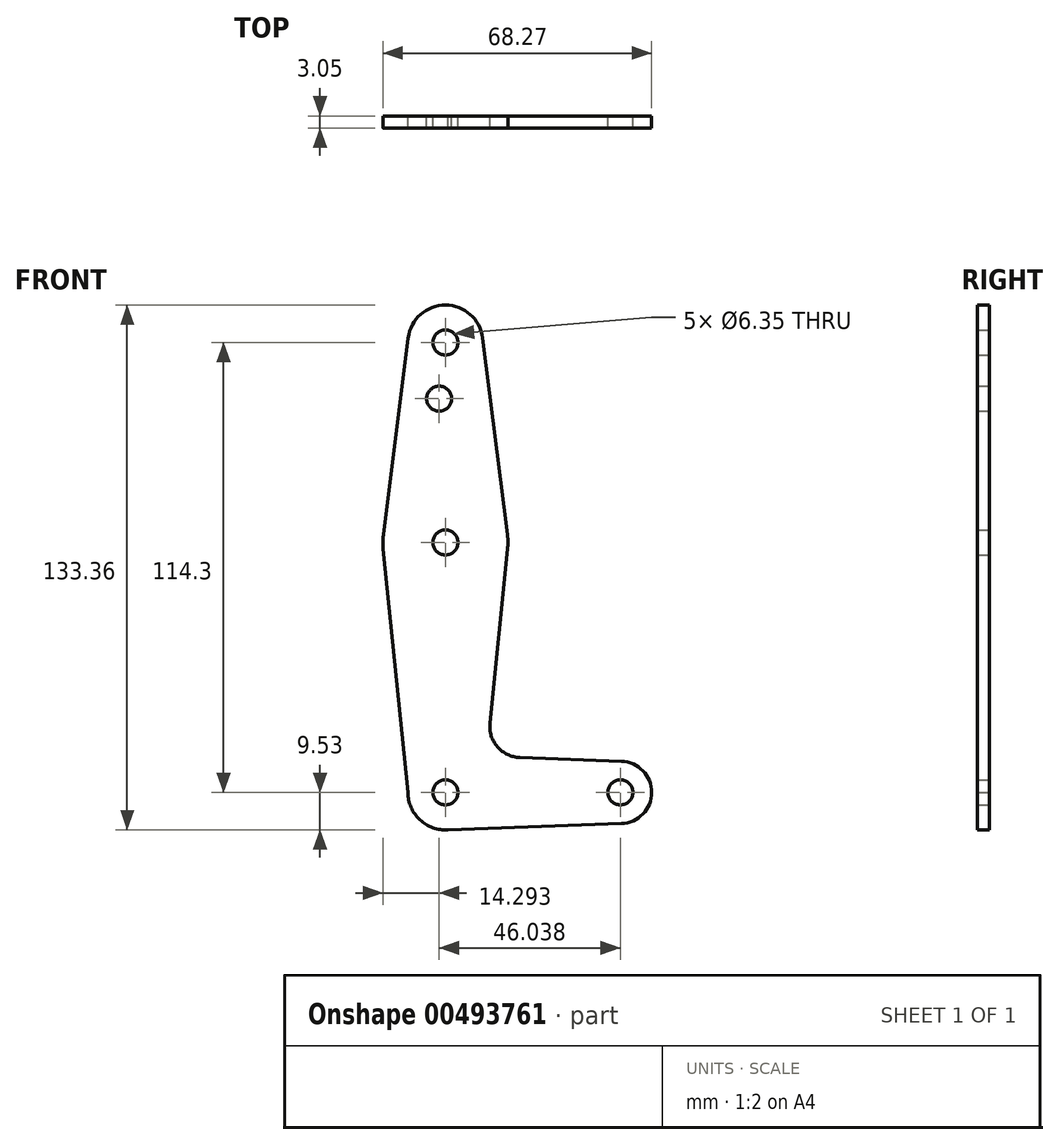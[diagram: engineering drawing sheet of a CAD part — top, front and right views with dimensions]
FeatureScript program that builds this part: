
annotation { "Feature Type Name" : "Feature", "Feature Type Description" : "" }
export const myFeature = defineFeature(function(context is Context, id is Id, definition is map)
    precondition{}
    {
        {
            var Q0;
            Q0=qCreatedBy(makeId("Front.planeOp"),FACE);
            var sketch = newSketch(context, id + "F0", { "sketchPlane" : qUnion([Q0])});
            skLineSegment(sketch, "E0", {"start": v(0, 0) * mm, "end": v(0, 114.3) * mm, "construction": true});
            skCircle(sketch, "E1", {"center": v(0, 114.3) * mm, "radius": 9.53 * mm});
            skCircle(sketch, "E2", {"center": v(0, 63.5) * mm, "radius": 15.88 * mm});
            skCircle(sketch, "E3", {"center": v(0, 0) * mm, "radius": 9.53 * mm});
            skLineSegment(sketch, "E4", {"start": v(0, 0) * mm, "end": v(44.45, 0) * mm, "construction": true});
            skCircle(sketch, "E5", {"center": v(44.45, 0) * mm, "radius": 7.94 * mm});
            skLineSegment(sketch, "E6", {"start": v(-15.75, 65.48) * mm, "end": v(-9.45, 115.5) * mm});
            skLineSegment(sketch, "E7", {"start": v(9.45, 115.5) * mm, "end": v(15.75, 65.48) * mm});
            skLineSegment(sketch, "E8", {"start": v(18.93, 8.85) * mm, "end": v(44.73, 7.93) * mm});
            skLineSegment(sketch, "E9", {"start": v(0, -9.53) * mm, "end": v(44.73, -7.93) * mm});
            skLineSegment(sketch, "E10", {"start": v(11.3, 17.6) * mm, "end": v(15.8, 61.9) * mm});
            skLineSegment(sketch, "E11", {"start": v(-9.52, 0) * mm, "end": v(-15.8, 61.9) * mm});
            skCircle(sketch, "E12", {"center": v(0, 114.3) * mm, "radius": 3.18 * mm});
            skCircle(sketch, "E13", {"center": v(0, 63.5) * mm, "radius": 3.18 * mm});
            skCircle(sketch, "E14", {"center": v(0, 0) * mm, "radius": 3.18 * mm});
            skCircle(sketch, "E15", {"center": v(44.45, 0) * mm, "radius": 3.18 * mm});
            skCircle(sketch, "E16", {"center": v(-1.59, 100.03) * mm, "radius": 3.18 * mm});
            skPoint(sketch, "E17.newPointA", {"position": v(9.52, 0) * mm});
            skArc(sketch, "E17.filletArc", {"start": v(11.3, 17.6) * mm, "mid": v(13.22, 11.57) * mm, "end": v(18.93, 8.85) * mm});
            skSolve(sketch);
        }
        {
            var Q0;
            Q0 = qSketchRegion(id + "F0", true);
            var Q1;
            {var subQ1=sQuery(id+"F0.wireOp",EDGE,"E6");Q1=makeQuery(id+"F0.imprint","IMPRINT",FACE,{"disambiguationData":[TD([[makeQuery(id+"F0.imprint","IMPRINT",EDGE,{"derivedFrom":subQ1}),-1.0]])]});}
            extrude(context, id + "F1", {"entities" : qUnion([Q0, Q1]), "depth" : 3.05 * mm});
        }
    });
